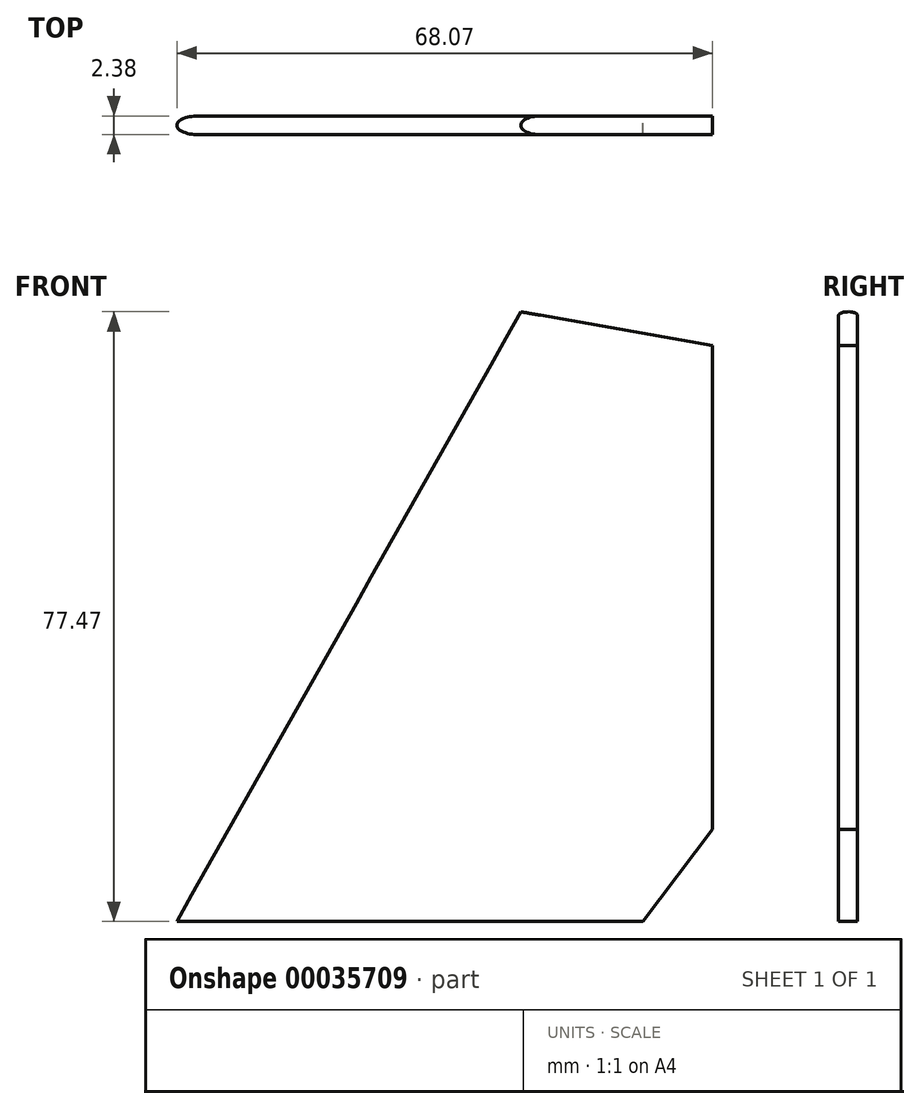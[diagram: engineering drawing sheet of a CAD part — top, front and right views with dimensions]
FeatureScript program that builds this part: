
annotation { "Feature Type Name" : "Feature", "Feature Type Description" : "" }
export const myFeature = defineFeature(function(context is Context, id is Id, definition is map)
    precondition{}
    {
        {
            var Q0;
            Q0=qCreatedBy(makeId("Front.planeOp"),FACE);
            var sketch = newSketch(context, id + "F0", { "sketchPlane" : qUnion([Q0])});
            skLineSegment(sketch, "E0", {"start": v(59.18, 0) * mm, "end": v(0, 0) * mm});
            skLineSegment(sketch, "E1", {"start": v(61.47, 64.82) * mm, "end": v(61.47, 11.68) * mm});
            skLineSegment(sketch, "E2", {"start": v(56.13, 57.67) * mm, "end": v(56.13, 11.68) * mm});
            skLineSegment(sketch, "E3", {"start": v(68.07, 73.15) * mm, "end": v(68.07, 11.68) * mm});
            skLineSegment(sketch, "E4", {"start": v(0, 0) * mm, "end": v(43.69, 77.47) * mm});
            skLineSegment(sketch, "E5", {"start": v(68.07, 11.68) * mm, "end": v(6.59, 11.68) * mm, "construction": true});
            skLineSegment(sketch, "E6", {"start": v(38.82, 68.83) * mm, "end": v(61.47, 64.82) * mm});
            skLineSegment(sketch, "E7", {"start": v(34.66, 61.47) * mm, "end": v(56.13, 57.67) * mm});
            skLineSegment(sketch, "E8", {"start": v(56.13, 11.68) * mm, "end": v(47.24, 0) * mm});
            skLineSegment(sketch, "E9", {"start": v(43.69, 77.47) * mm, "end": v(68.07, 73.15) * mm});
            skLineSegment(sketch, "E10", {"start": v(61.47, 11.68) * mm, "end": v(52.58, 0) * mm});
            skLineSegment(sketch, "E11", {"start": v(68.07, 11.68) * mm, "end": v(59.18, 0) * mm});
            skSolve(sketch);
        }
        {
            var Q0;
            Q0=makeQuery(id+"F0.imprint","IMPRINT",FACE,{"disambiguationData":[TD([[makeQuery(id+"F0.imprint","IMPRINT",EDGE,{"derivedFrom":sQuery(id+"F0.wireOp",EDGE,"E2")}),-1.0]])]});
            var Q1;
            Q1=makeQuery(id+"F0.imprint","IMPRINT",FACE,{"disambiguationData":[TD([[makeQuery(id+"F0.imprint","IMPRINT",EDGE,{"derivedFrom":sQuery(id+"F0.wireOp",EDGE,"E1")}),-1.0]])]});
            var Q2;
            Q2=makeQuery(id+"F0.imprint","IMPRINT",FACE,{"disambiguationData":[TD([[makeQuery(id+"F0.imprint","IMPRINT",EDGE,{"derivedFrom":sQuery(id+"F0.wireOp",EDGE,"E1")}),1.0]])]});
            extrude(context, id + "F1", {"entities" : qUnion([Q0, Q1, Q2]), "depth" : 2.38 * mm, "symmetric" : true});
        }
        {
            var Q0;
            Q0=sQuery(id+"F0.wireOp",EDGE,"E4");
            var Q1;
            Q1=sQuery(id+"F0.wireOp",VERTEX,"E4.start");
            cPlane(context, id + "F2", {"entities" : qUnion([Q0, Q1]), "cplaneType" : CPlaneType.LINE_POINT, "offset" : 152.4 * mm, "width" : 152.4 * mm, "height" : 152.4 * mm});
        }
        {
            var Q0;
            Q0=qCreatedBy(id+"F2.planeOp",FACE);
            var sketch = newSketch(context, id + "F3", { "sketchPlane" : qUnion([Q0])});
            skLineSegment(sketch, "E12", {"start": v(23.36, 1.2) * mm, "end": v(23.36, 12.7) * mm});
            skLineSegment(sketch, "E13.1", {"start": v(2.38, 1.2) * mm, "end": v(23.36, 1.2) * mm});
            skLineSegment(sketch, "E14", {"start": v(-12.7, -12.7) * mm, "end": v(23.36, -12.7) * mm});
            skLineSegment(sketch, "E15", {"start": v(23.36, -12.7) * mm, "end": v(23.36, -1.2) * mm});
            skLineSegment(sketch, "E16", {"start": v(-12.7, 12.7) * mm, "end": v(-12.7, -12.7) * mm});
            skLineSegment(sketch, "E17", {"start": v(23.36, 12.7) * mm, "end": v(-12.7, 12.7) * mm});
            skLineSegment(sketch, "E13.2", {"start": v(2.38, -1.2) * mm, "end": v(23.36, -1.2) * mm});
            skPoint(sketch, "E18.orphan", {"position": v(0, 1.2) * mm});
            skEllipticalArc(sketch, "E19", {});
            skLineSegment(sketch, "E20", {"start": v(2.38, 1.2) * mm, "end": v(2.38, -1.2) * mm, "construction": true});
            skLineSegment(sketch, "E21", {"start": v(0, 0) * mm, "end": v(2.38, 0) * mm});
            skLineSegment(sketch, "E22", {"start": v(2.38, 0) * mm, "end": v(0, 0) * mm, "construction": true});
            const initialGuessF3  = {"E19": [0.002381250000000007, 0, -1, 0, 0.00238125, 0.001190625, 4.71238898038469, 1.5707963267948966]};
            skSetInitialGuess(sketch, initialGuessF3);
            skSolve(sketch);
        }
        {
            var Q0;
            Q0 = qSketchRegion(id + "F3", true);
            extrude(context, id + "F4", {"entities" : qUnion([Q0]), "operationType" : NewBodyOperationType.REMOVE, "endBound" : BoundingType.THROUGH_ALL, "depth" : 25.4 * mm});
        }
    });
